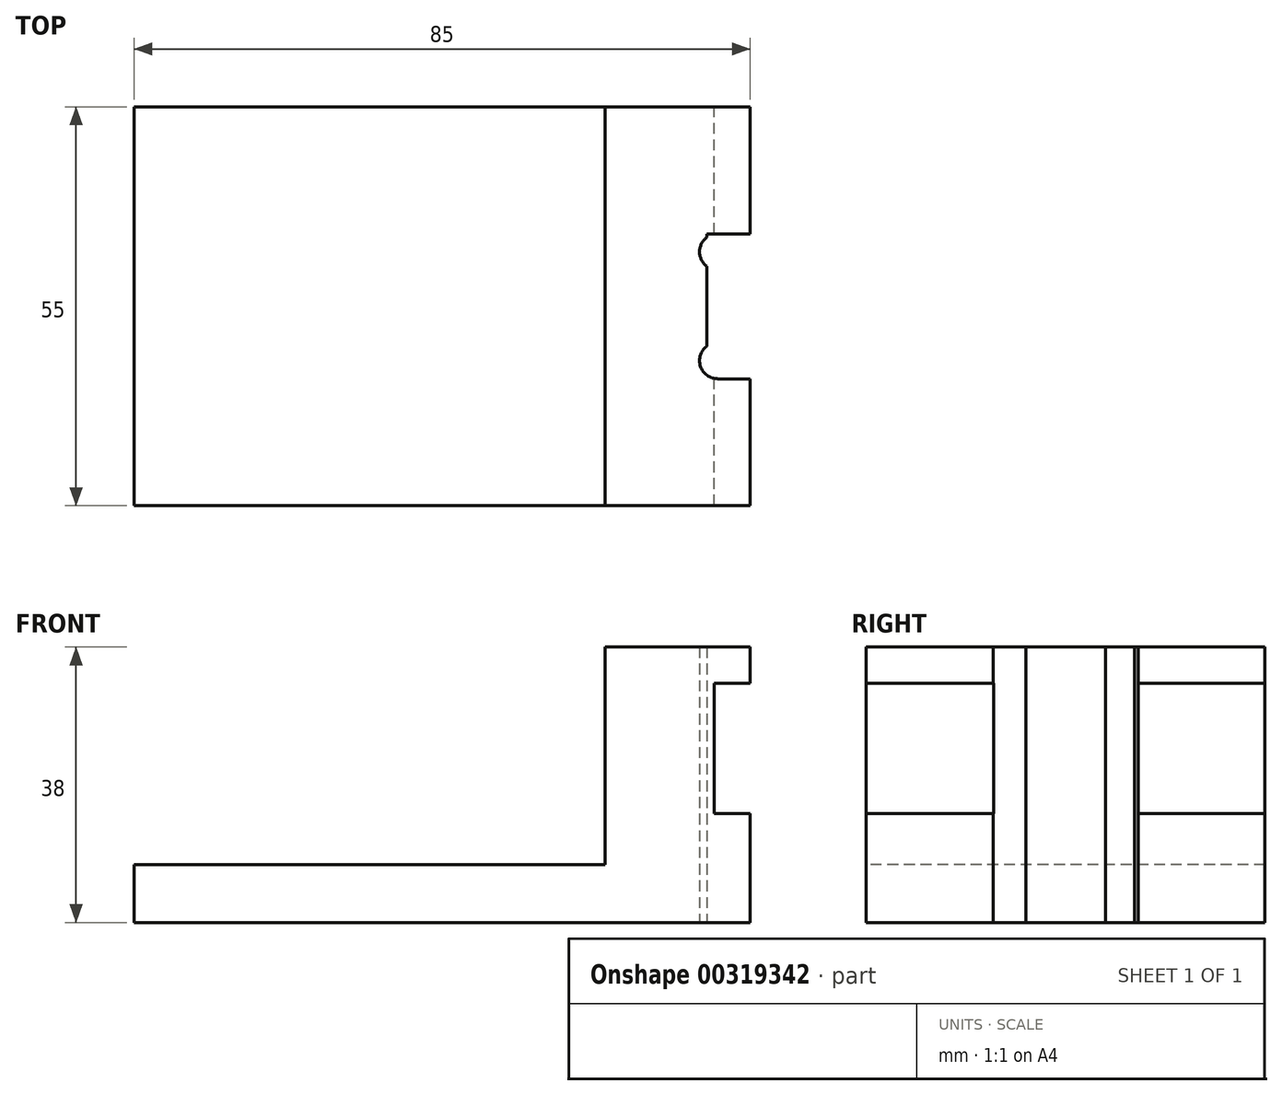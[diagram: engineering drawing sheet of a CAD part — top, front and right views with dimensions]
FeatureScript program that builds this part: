
annotation { "Feature Type Name" : "Feature", "Feature Type Description" : "" }
export const myFeature = defineFeature(function(context is Context, id is Id, definition is map)
    precondition{}
    {
        {
            var Q0;
            Q0=qCreatedBy(makeId("Front.planeOp"),FACE);
            var sketch = newSketch(context, id + "F0", { "sketchPlane" : qUnion([Q0])});
            skLineSegment(sketch, "E0.bottom", {"start": v(0, 0) * mm, "end": v(-85, 0) * mm});
            skLineSegment(sketch, "E0.top", {"start": v(0, 38) * mm, "end": v(-85, 38) * mm});
            skLineSegment(sketch, "E0.left", {"start": v(0, 0) * mm, "end": v(0, 38) * mm});
            skLineSegment(sketch, "E0.right", {"start": v(-85, 0) * mm, "end": v(-85, 38) * mm});
            skSolve(sketch);
        }
        {
            var Q0;
            Q0 = qSketchRegion(id + "F0", true);
            extrude(context, id + "F1", {"entities" : qUnion([Q0]), "endBound" : BoundingType.SYMMETRIC, "depth" : 55 * mm});
        }
        {
            var Q0;
            Q0=qCreatedBy(makeId("Front.planeOp"),FACE);
            var sketch = newSketch(context, id + "F2", { "sketchPlane" : qUnion([Q0])});
            skLineSegment(sketch, "E1.bottom", {"start": v(-20, 8) * mm, "end": v(-85, 8) * mm});
            skLineSegment(sketch, "E1.top", {"start": v(-20, 38) * mm, "end": v(-85, 38) * mm});
            skLineSegment(sketch, "E1.left", {"start": v(-20, 8) * mm, "end": v(-20, 38) * mm});
            skLineSegment(sketch, "E1.right", {"start": v(-85, 8) * mm, "end": v(-85, 38) * mm});
            skSolve(sketch);
        }
        {
            var Q0;
            Q0 = qSketchRegion(id + "F2", true);
            extrude(context, id + "F3", {"entities" : qUnion([Q0]), "operationType" : NewBodyOperationType.REMOVE, "endBound" : BoundingType.THROUGH_ALL, "oppositeDirection" : true, "depth" : 25 * mm, "hasSecondDirection" : true, "secondDirectionBound" : SecondDirectionBoundingType.THROUGH_ALL, "secondDirectionOppositeDirection" : false, "secondDirectionDepth" : 25 * mm});
        }
        {
            var Q0;
            Q0=qCreatedBy(makeId("Front.planeOp"),FACE);
            var sketch = newSketch(context, id + "F4", { "sketchPlane" : qUnion([Q0])});
            skLineSegment(sketch, "E2.bottom", {"start": v(0, 15) * mm, "end": v(-5, 15) * mm});
            skLineSegment(sketch, "E2.top", {"start": v(0, 33) * mm, "end": v(-5, 33) * mm});
            skLineSegment(sketch, "E2.left", {"start": v(0, 15) * mm, "end": v(0, 33) * mm});
            skLineSegment(sketch, "E2.right", {"start": v(-5, 15) * mm, "end": v(-5, 33) * mm});
            skSolve(sketch);
        }
        {
            var Q0;
            Q0 = qSketchRegion(id + "F4", true);
            extrude(context, id + "F5", {"entities" : qUnion([Q0]), "operationType" : NewBodyOperationType.REMOVE, "endBound" : BoundingType.THROUGH_ALL, "depth" : 25 * mm, "hasSecondDirection" : true, "secondDirectionBound" : SecondDirectionBoundingType.THROUGH_ALL, "secondDirectionOppositeDirection" : true, "secondDirectionDepth" : 25 * mm});
        }
        {
            var Q0;
            Q0=qCreatedBy(makeId("Top.planeOp"),FACE);
            var sketch = newSketch(context, id + "F6", { "sketchPlane" : qUnion([Q0])});
            skLineSegment(sketch, "E3", {"start": v(0, -24.74) * mm, "end": v(0, 16.45) * mm, "construction": true});
            skLineSegment(sketch, "E4.bottom", {"start": v(-6, 10) * mm, "end": v(6, 10) * mm});
            skLineSegment(sketch, "E4.top", {"start": v(-4.5, -10) * mm, "end": v(4.5, -10) * mm});
            skLineSegment(sketch, "E4.left", {"start": v(-6, 10) * mm, "end": v(-6, -5.5) * mm});
            skLineSegment(sketch, "E4.right", {"start": v(6, 10) * mm, "end": v(6, -5.5) * mm});
            skPoint(sketch, "E4.middle", {"position": v(0, 0) * mm});
            skLineSegment(sketch, "E5", {"start": v(-27.5, 0) * mm, "end": v(27.5, 0) * mm, "construction": true});
            skLineSegment(sketch, "E6", {"start": v(-4.5, 7.5) * mm, "end": v(4.5, 7.5) * mm, "construction": true});
            skPoint(sketch, "E7", {"position": v(0, 7.5) * mm});
            skArc(sketch, "E8.0.startCap", {"start": v(-4.5, 5) * mm, "mid": v(-7, 7.5) * mm, "end": v(-4.5, 10) * mm});
            skArc(sketch, "E8.0.endCap", {"start": v(4.5, 10) * mm, "mid": v(7, 7.5) * mm, "end": v(4.5, 5) * mm});
            skLineSegment(sketch, "E8.0.left", {"start": v(-4.5, 10) * mm, "end": v(4.5, 10) * mm});
            skLineSegment(sketch, "E8.0.right", {"start": v(-4.5, 5) * mm, "end": v(4.5, 5) * mm});
            skArc(sketch, "E9.MirrorCS", {"start": v(-6, -5.5) * mm, "mid": v(-6.87, -8.3) * mm, "end": v(-4.5, -10) * mm});
            skArc(sketch, "E10.MirrorCS", {"start": v(4.5, -10) * mm, "mid": v(6.87, -8.3) * mm, "end": v(6, -5.5) * mm});
            skLineSegment(sketch, "E11.MirrorCS", {"start": v(-4.5, -7.5) * mm, "end": v(4.5, -7.5) * mm, "construction": true});
            skPoint(sketch, "E12.trimOffspring.end.orphan", {"position": v(-6, -10) * mm});
            skPoint(sketch, "E13.orphan", {"position": v(6, -10) * mm});
            skPoint(sketch, "E14.orphan", {"position": v(4.5, -5) * mm});
            skPoint(sketch, "E15.orphan", {"position": v(-4.5, -5) * mm});
            skSolve(sketch);
        }
        {
            var Q0;
            Q0 = qSketchRegion(id + "F6", true);
            extrude(context, id + "F7", {"entities" : qUnion([Q0]), "operationType" : NewBodyOperationType.REMOVE, "endBound" : BoundingType.THROUGH_ALL, "depth" : 25 * mm});
        }
    });
